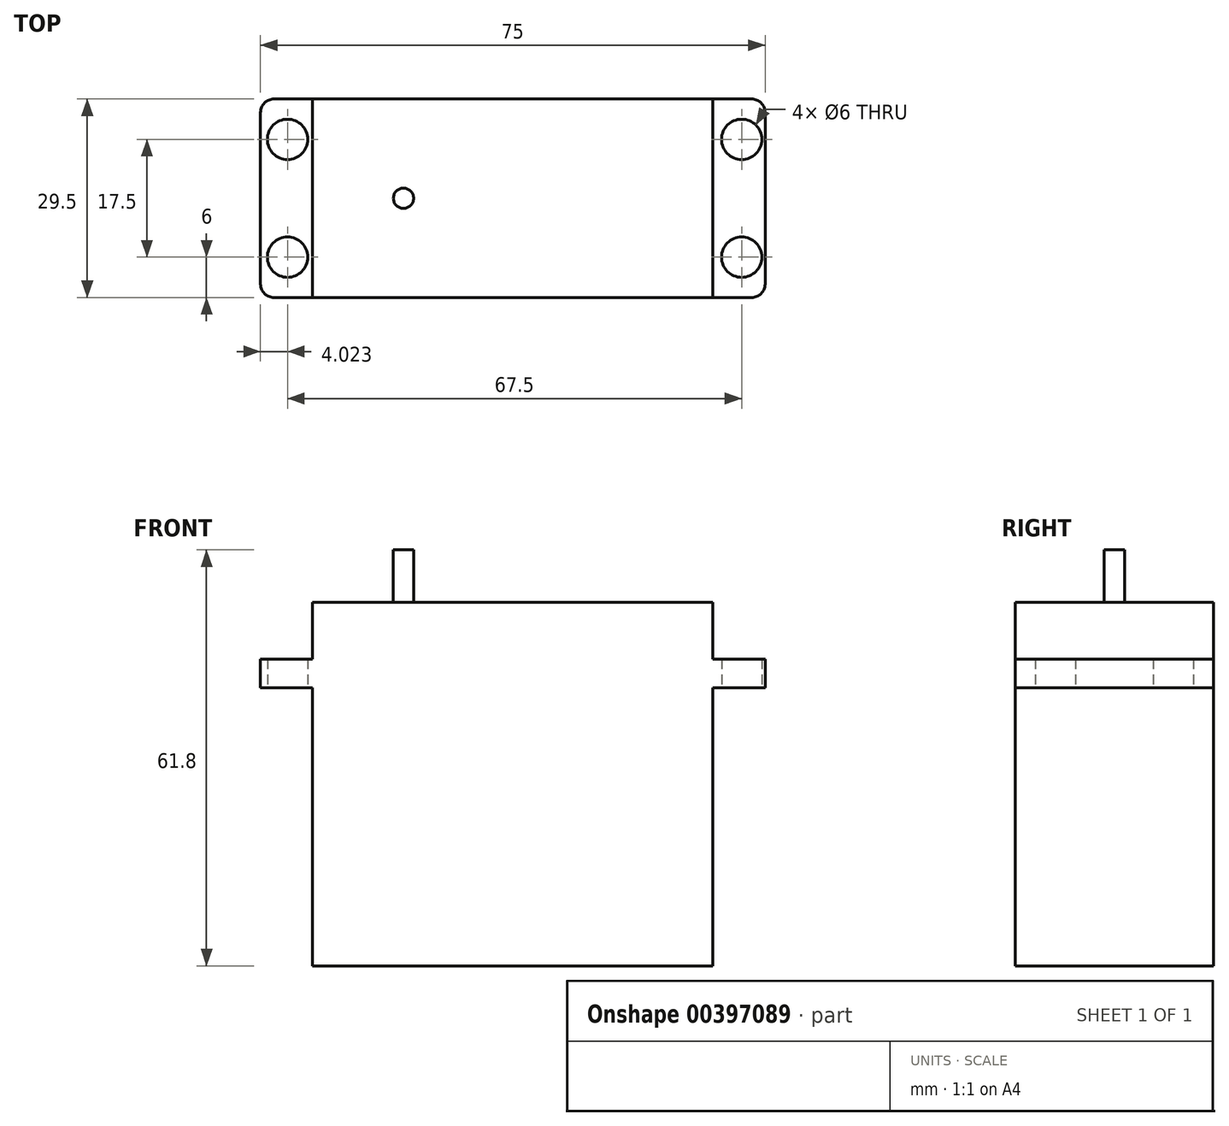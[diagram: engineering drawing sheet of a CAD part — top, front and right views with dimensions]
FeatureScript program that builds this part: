
annotation { "Feature Type Name" : "Feature", "Feature Type Description" : "" }
export const myFeature = defineFeature(function(context is Context, id is Id, definition is map)
    precondition{}
    {
        {
            var Q0;
            Q0=qCreatedBy(makeId("Top.planeOp"),FACE);
            var sketch = newSketch(context, id + "F0", { "sketchPlane" : qUnion([Q0])});
            skLineSegment(sketch, "E0.bottom", {"start": v(29.75, -14.75) * mm, "end": v(-29.75, -14.75) * mm});
            skLineSegment(sketch, "E0.top", {"start": v(29.75, 14.75) * mm, "end": v(-29.75, 14.75) * mm});
            skLineSegment(sketch, "E0.left", {"start": v(29.75, -14.75) * mm, "end": v(29.75, 14.75) * mm});
            skLineSegment(sketch, "E0.right", {"start": v(-29.75, -14.75) * mm, "end": v(-29.75, 14.75) * mm});
            skPoint(sketch, "E0.middle", {"position": v(0, 0) * mm});
            skSolve(sketch);
        }
        {
            var Q0;
            Q0=qSketchRegion(id+"F0",true);
            extrude(context, id + "F1", {"entities" : qUnion([Q0]), "depth" : 12.7 * mm, "hasSecondDirection" : true, "secondDirectionOppositeDirection" : true, "secondDirectionDepth" : 41.3 * mm});
        }
        {
            var Q0;
            Q0=qCreatedBy(makeId("Top.planeOp"),FACE);
            var sketch = newSketch(context, id + "F2", { "sketchPlane" : qUnion([Q0])});
            skLineSegment(sketch, "E1.bottom", {"start": v(35.5, -14.75) * mm, "end": v(-35.5, -14.75) * mm});
            skLineSegment(sketch, "E1.top", {"start": v(35.5, 14.75) * mm, "end": v(-35.5, 14.75) * mm});
            skLineSegment(sketch, "E1.left", {"start": v(37.5, -12.75) * mm, "end": v(37.5, 12.75) * mm});
            skLineSegment(sketch, "E1.right", {"start": v(-37.5, -12.75) * mm, "end": v(-37.5, 12.75) * mm});
            skPoint(sketch, "E1.middle", {"position": v(0, 0) * mm});
            skPoint(sketch, "E2.visualSharp", {"position": v(-37.5, 14.75) * mm});
            skArc(sketch, "E2.filletArc", {"start": v(-35.5, 14.75) * mm, "mid": v(-36.91, 14.16) * mm, "end": v(-37.5, 12.75) * mm});
            skPoint(sketch, "E3.visualSharp", {"position": v(-37.5, -14.75) * mm});
            skArc(sketch, "E3.filletArc", {"start": v(-37.5, -12.75) * mm, "mid": v(-36.91, -14.16) * mm, "end": v(-35.5, -14.75) * mm});
            skPoint(sketch, "E4.visualSharp", {"position": v(37.5, -14.75) * mm});
            skArc(sketch, "E4.filletArc", {"start": v(35.5, -14.75) * mm, "mid": v(36.91, -14.16) * mm, "end": v(37.5, -12.75) * mm});
            skPoint(sketch, "E5.visualSharp", {"position": v(37.5, 14.75) * mm});
            skArc(sketch, "E5.filletArc", {"start": v(37.5, 12.75) * mm, "mid": v(36.91, 14.16) * mm, "end": v(35.5, 14.75) * mm});
            skCircle(sketch, "E6", {"center": v(-33.48, 8.75) * mm, "radius": 3 * mm});
            skCircle(sketch, "E7.1.0.0", {"center": v(34.02, 8.75) * mm, "radius": 3 * mm});
            skLineSegment(sketch, "E7.direction1", {"start": v(-33.48, 8.75) * mm, "end": v(34.02, 8.75) * mm, "construction": true});
            skCircle(sketch, "E8.1.0.0", {"center": v(-33.48, -8.75) * mm, "radius": 3 * mm});
            skCircle(sketch, "E8.1.0.1", {"center": v(34.02, -8.75) * mm, "radius": 3 * mm});
            skLineSegment(sketch, "E8.direction1", {"start": v(-33.48, 8.75) * mm, "end": v(-33.48, -8.75) * mm, "construction": true});
            skSolve(sketch);
        }
        {
            var Q0;
            Q0=qSketchRegion(id+"F2",true);
            extrude(context, id + "F3", {"entities" : qUnion([Q0]), "operationType" : NewBodyOperationType.ADD, "depth" : 4.3 * mm});
        }
        {
            var Q0;
            Q0=makeQuery(id+"F1.opExtrude","CAP_FACE",FACE,{"disambiguationData":[OSD([sQuery(id+"F0.wireOp",EDGE,"E0.bottom"),sQuery(id+"F0.wireOp",EDGE,"E0.top"),sQuery(id+"F0.wireOp",EDGE,"E0.left"),sQuery(id+"F0.wireOp",EDGE,"E0.right")])],"isStart":false});
            var sketch = newSketch(context, id + "F4", { "sketchPlane" : qUnion([Q0])});
            skPoint(sketch, "E9", {"position": v(-16.25, 0) * mm});
            skPoint(sketch, "E10", {"position": v(-29.75, 0) * mm});
            skCircle(sketch, "E11", {"center": v(-16.25, 0) * mm, "radius": 1.5 * mm});
            skSolve(sketch);
        }
        {
            var Q0;
            Q0=qSketchRegion(id+"F4",true);
            extrude(context, id + "F5", {"entities" : qUnion([Q0]), "operationType" : NewBodyOperationType.ADD, "depth" : 7.8 * mm});
        }
    });
